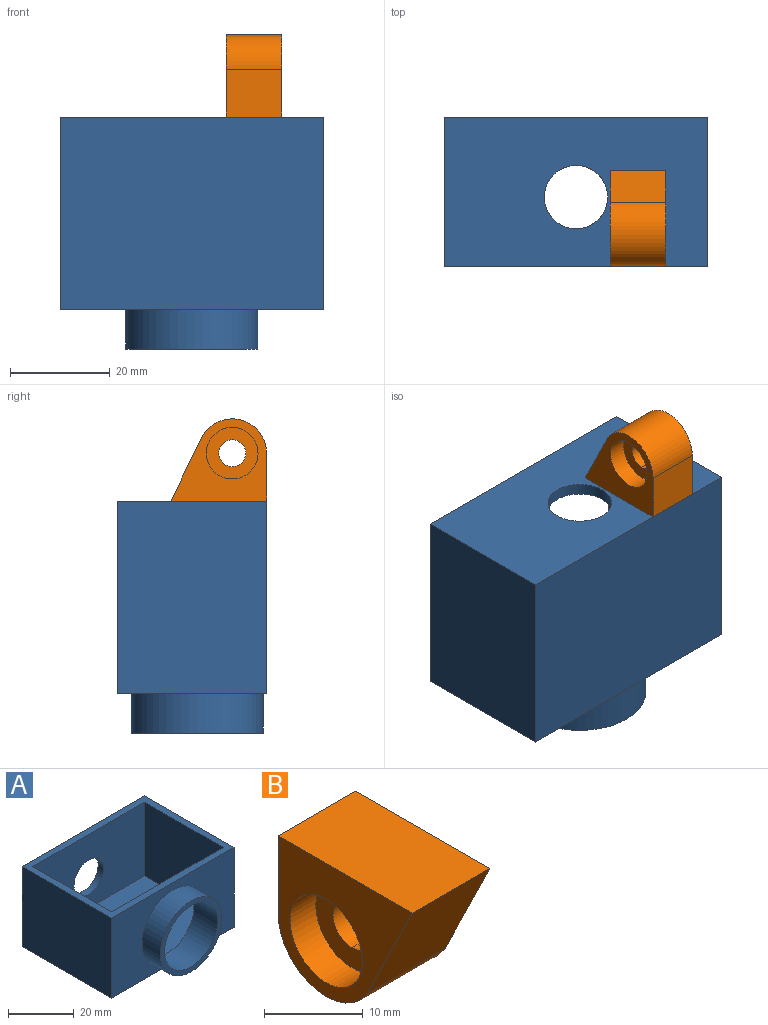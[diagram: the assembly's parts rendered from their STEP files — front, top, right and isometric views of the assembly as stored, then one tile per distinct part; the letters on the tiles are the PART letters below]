
ASSEMBLY  parts=2 mates=2
PART A: 15 faces, bbox 52.9x46.5x29.9 mm
  f0: plane 52.89x38.58mm, normal (0,0,-1), area 2040.9mm2, adj f4,f5,f6,f7
  f1: plane 33.92x27.56mm, normal (-1,0,0), area 934.8mm2, adj f2,f8,f9,f10
  f2: plane 48.23x27.56mm, normal (0,1,0), area 917.9mm2, adj f1,f3,f9,f10,f12
  f3: plane 33.92x27.56mm, normal (1,0,0), area 934.8mm2, adj f2,f8,f9,f10
  f4: plane 52.89x29.89mm, normal (0,-1,0), area 1029.6mm2, adj f0,f5,f7,f9,f13
  f5: plane 38.58x29.89mm, normal (1,0,0), area 1153.4mm2, adj f0,f4,f6,f9
  f6: plane 52.89x29.89mm, normal (0,1,0), area 1454mm2, adj f0,f5,f7,f9,f11
  f7: plane 38.58x29.89mm, normal (-1,0,0), area 1153.4mm2, adj f0,f4,f6,f9
  f8: plane 48.23x27.56mm, normal (0,-1,0), area 1202.1mm2, adj f1,f3,f9,f10,f11
  f9: plane 52.89x38.58mm, normal (0,0,1), area 404.9mm2, adj f1,f2,f3,f4,f5,f6,f7,f8
  f10: plane 48.23x33.92mm, normal (0,0,1), area 1636mm2, adj f1,f2,f3,f8
  f11: cylinder r=6.36mm len=12.72mm, axis (0,1,0), area 93.2mm2, adj f6,f8
  f12: cylinder r=11.44mm len=22.89mm, axis (0,1,0), area 739.2mm2, adj f2,f14
  f13: cylinder r=13.25mm len=26.5mm, axis (0,1,0), area 661.9mm2, adj f4,f14
  f14: plane 26.5x26.5mm, normal (0,-1,0), area 140.2mm2, adj f12,f13
PART B: 152 faces, bbox 11.1x19.2x16.5 mm
  f0: cylinder r=5.18mm len=10.37mm, axis (-1,0,0), area 120.8mm2, adj f148,f149
  f1: plane 12.72x12.72mm, normal (1,0,0), area 68.7mm2, adj f2,f3,f7,f8,f9,f10,f11,f13
  f2: cylinder r=2.7mm len=6.36mm, axis (1,0,0), area 54.2mm2, adj f1,f3,f149
  f3: cylinder r=2.7mm len=6.36mm, axis (1,0,0), area 54.2mm2, adj f1,f2,f149
  f4: plane 13.08x11.13mm, normal (0,-0.9,-0.44), area 162mm2, adj f5,f6,f148,f150
  f5: cylinder r=6.88mm len=12.82mm, axis (1,0,0), area 200mm2, adj f4,f6,f148,f151
  f6: plane 19.21x16.49mm, normal (1,0,0), area 110.1mm2, adj f4,f5,f7,f150,f151
  f7: cylinder r=6.36mm len=12.72mm, axis (1,0,0), area 42.4mm2, adj f1,f6
  f8: plane 1.06x0.85mm, normal (0,0,1), area 0.9mm2, adj f1,f9,f11,f12
  f9: plane 1.48x1.06mm, normal (0,1,0), area 1.6mm2, adj f1,f8,f10,f12
  f10: plane 1.06x0.85mm, normal (0,0,-1), area 0.9mm2, adj f1,f9,f11,f12
  f11: plane 1.48x1.06mm, normal (0,-1,0), area 1.6mm2, adj f1,f8,f10,f12
  f12: plane 1.48x0.85mm, normal (1,0,0), area 1.3mm2, adj f8,f9,f10,f11
  f13: plane 1.45x1.06mm, normal (0,-0.97,0.22), area 1.6mm2, adj f1,f14,f16,f17
  f14: plane 1.06x0.83mm, normal (0,0.22,0.97), area 0.9mm2, adj f1,f13,f15,f17
  f15: plane 1.45x1.06mm, normal (0,0.97,-0.22), area 1.6mm2, adj f1,f14,f16,f17
  f16: plane 1.06x0.83mm, normal (0,-0.22,-0.97), area 0.9mm2, adj f1,f13,f15,f17
  f17: plane 1.64x1.16mm, normal (1,0,0), area 1.3mm2, adj f13,f14,f15,f16
  f18: plane 1.34x1.06mm, normal (0,-0.9,0.43), area 1.6mm2, adj f1,f19,f21,f22
  f19: plane 1.06x0.76mm, normal (0,0.43,0.9), area 0.9mm2, adj f1,f18,f20,f22
  f20: plane 1.34x1.06mm, normal (0,0.9,-0.43), area 1.6mm2, adj f1,f19,f21,f22
  f21: plane 1.06x0.76mm, normal (0,-0.43,-0.9), area 0.9mm2, adj f1,f18,f20,f22
  f22: plane 1.71x1.41mm, normal (1,0,0), area 1.3mm2, adj f18,f19,f20,f21
  f23: plane 1.16x1.06mm, normal (0,-0.78,0.62), area 1.6mm2, adj f1,f24,f26,f27
  f24: plane 1.06x0.66mm, normal (0,0.62,0.78), area 0.9mm2, adj f1,f23,f25,f27
  f25: plane 1.16x1.06mm, normal (0,0.78,-0.62), area 1.6mm2, adj f1,f24,f26,f27
  f26: plane 1.06x0.66mm, normal (0,-0.62,-0.78), area 0.9mm2, adj f1,f23,f25,f27
  f27: plane 1.69x1.59mm, normal (1,0,0), area 1.3mm2, adj f23,f24,f25,f26
  f28: plane 1.16x1.06mm, normal (0,-0.62,0.78), area 1.6mm2, adj f1,f29,f31,f32
  f29: plane 1.06x0.66mm, normal (0,0.78,0.62), area 0.9mm2, adj f1,f28,f30,f32
  f30: plane 1.16x1.06mm, normal (0,0.62,-0.78), area 1.6mm2, adj f1,f29,f31,f32
  f31: plane 1.06x0.66mm, normal (0,-0.78,-0.62), area 0.9mm2, adj f1,f28,f30,f32
  f32: plane 1.69x1.59mm, normal (1,0,0), area 1.3mm2, adj f28,f29,f30,f31
  f33: plane 1.34x1.06mm, normal (0,-0.43,0.9), area 1.6mm2, adj f1,f34,f36,f37
  f34: plane 1.06x0.76mm, normal (0,0.9,0.43), area 0.9mm2, adj f1,f33,f35,f37
  f35: plane 1.34x1.06mm, normal (0,0.43,-0.9), area 1.6mm2, adj f1,f34,f36,f37
  f36: plane 1.06x0.76mm, normal (0,-0.9,-0.43), area 0.9mm2, adj f1,f33,f35,f37
  f37: plane 1.71x1.41mm, normal (1,0,0), area 1.3mm2, adj f33,f34,f35,f36
  f38: plane 1.45x1.06mm, normal (0,-0.22,0.97), area 1.6mm2, adj f1,f39,f41,f42
  f39: plane 1.06x0.83mm, normal (0,0.97,0.22), area 0.9mm2, adj f1,f38,f40,f42
  f40: plane 1.45x1.06mm, normal (0,0.22,-0.97), area 1.6mm2, adj f1,f39,f41,f42
  f41: plane 1.06x0.83mm, normal (0,-0.97,-0.22), area 0.9mm2, adj f1,f38,f40,f42
  f42: plane 1.64x1.16mm, normal (1,0,0), area 1.3mm2, adj f38,f39,f40,f41
  f43: plane 1.48x1.06mm, normal (0,0,1), area 1.6mm2, adj f1,f44,f46,f47
  f44: plane 1.06x0.85mm, normal (0,1,0), area 0.9mm2, adj f1,f43,f45,f47
  f45: plane 1.48x1.06mm, normal (0,0,-1), area 1.6mm2, adj f1,f44,f46,f47
  f46: plane 1.06x0.85mm, normal (0,-1,0), area 0.9mm2, adj f1,f43,f45,f47
  f47: plane 1.48x0.85mm, normal (1,0,0), area 1.3mm2, adj f43,f44,f45,f46
  f48: plane 1.45x1.06mm, normal (0,0.22,0.97), area 1.6mm2, adj f1,f49,f51,f52
  f49: plane 1.06x0.83mm, normal (0,0.97,-0.22), area 0.9mm2, adj f1,f48,f50,f52
  f50: plane 1.45x1.06mm, normal (0,-0.22,-0.97), area 1.6mm2, adj f1,f49,f51,f52
  f51: plane 1.06x0.83mm, normal (0,-0.97,0.22), area 0.9mm2, adj f1,f48,f50,f52
  f52: plane 1.64x1.16mm, normal (1,0,0), area 1.3mm2, adj f48,f49,f50,f51
  f53: plane 1.34x1.06mm, normal (0,0.43,0.9), area 1.6mm2, adj f1,f54,f56,f57
  f54: plane 1.06x0.76mm, normal (0,0.9,-0.43), area 0.9mm2, adj f1,f53,f55,f57
  f55: plane 1.34x1.06mm, normal (0,-0.43,-0.9), area 1.6mm2, adj f1,f54,f56,f57
  f56: plane 1.06x0.76mm, normal (0,-0.9,0.43), area 0.9mm2, adj f1,f53,f55,f57
  f57: plane 1.71x1.41mm, normal (1,0,0), area 1.3mm2, adj f53,f54,f55,f56
  f58: plane 1.16x1.06mm, normal (0,0.62,0.78), area 1.6mm2, adj f1,f59,f61,f62
  f59: plane 1.06x0.66mm, normal (0,0.78,-0.62), area 0.9mm2, adj f1,f58,f60,f62
  f60: plane 1.16x1.06mm, normal (0,-0.62,-0.78), area 1.6mm2, adj f1,f59,f61,f62
  f61: plane 1.06x0.66mm, normal (0,-0.78,0.62), area 0.9mm2, adj f1,f58,f60,f62
  f62: plane 1.69x1.59mm, normal (1,0,0), area 1.3mm2, adj f58,f59,f60,f61
  f63: plane 1.16x1.06mm, normal (0,0.78,0.62), area 1.6mm2, adj f1,f64,f66,f67
  f64: plane 1.06x0.66mm, normal (0,0.62,-0.78), area 0.9mm2, adj f1,f63,f65,f67
  f65: plane 1.16x1.06mm, normal (0,-0.78,-0.62), area 1.6mm2, adj f1,f64,f66,f67
  f66: plane 1.06x0.66mm, normal (0,-0.62,0.78), area 0.9mm2, adj f1,f63,f65,f67
  f67: plane 1.69x1.59mm, normal (1,0,0), area 1.3mm2, adj f63,f64,f65,f66
  f68: plane 1.34x1.06mm, normal (0,0.9,0.43), area 1.6mm2, adj f1,f69,f71,f72
  f69: plane 1.06x0.76mm, normal (0,0.43,-0.9), area 0.9mm2, adj f1,f68,f70,f72
  f70: plane 1.34x1.06mm, normal (0,-0.9,-0.43), area 1.6mm2, adj f1,f69,f71,f72
  f71: plane 1.06x0.76mm, normal (0,-0.43,0.9), area 0.9mm2, adj f1,f68,f70,f72
  f72: plane 1.71x1.41mm, normal (1,0,0), area 1.3mm2, adj f68,f69,f70,f71
  f73: plane 1.45x1.06mm, normal (0,0.97,0.22), area 1.6mm2, adj f1,f74,f76,f77
  f74: plane 1.06x0.83mm, normal (0,0.22,-0.97), area 0.9mm2, adj f1,f73,f75,f77
  f75: plane 1.45x1.06mm, normal (0,-0.97,-0.22), area 1.6mm2, adj f1,f74,f76,f77
  f76: plane 1.06x0.83mm, normal (0,-0.22,0.97), area 0.9mm2, adj f1,f73,f75,f77
  f77: plane 1.64x1.16mm, normal (1,0,0), area 1.3mm2, adj f73,f74,f75,f76
  f78: plane 1.48x1.06mm, normal (0,1,0), area 1.6mm2, adj f1,f79,f81,f82
  f79: plane 1.06x0.85mm, normal (0,0,-1), area 0.9mm2, adj f1,f78,f80,f82
  f80: plane 1.48x1.06mm, normal (0,-1,0), area 1.6mm2, adj f1,f79,f81,f82
  f81: plane 1.06x0.85mm, normal (0,0,1), area 0.9mm2, adj f1,f78,f80,f82
  f82: plane 1.48x0.85mm, normal (1,0,0), area 1.3mm2, adj f78,f79,f80,f81
  f83: plane 1.45x1.06mm, normal (0,0.97,-0.22), area 1.6mm2, adj f1,f84,f86,f87
  f84: plane 1.06x0.83mm, normal (0,-0.22,-0.97), area 0.9mm2, adj f1,f83,f85,f87
  f85: plane 1.45x1.06mm, normal (0,-0.97,0.22), area 1.6mm2, adj f1,f84,f86,f87
  f86: plane 1.06x0.83mm, normal (0,0.22,0.97), area 0.9mm2, adj f1,f83,f85,f87
  f87: plane 1.64x1.16mm, normal (1,0,0), area 1.3mm2, adj f83,f84,f85,f86
  f88: plane 1.34x1.06mm, normal (0,0.9,-0.43), area 1.6mm2, adj f1,f89,f91,f92
  f89: plane 1.06x0.76mm, normal (0,-0.43,-0.9), area 0.9mm2, adj f1,f88,f90,f92
  f90: plane 1.34x1.06mm, normal (0,-0.9,0.43), area 1.6mm2, adj f1,f89,f91,f92
  f91: plane 1.06x0.76mm, normal (0,0.43,0.9), area 0.9mm2, adj f1,f88,f90,f92
  f92: plane 1.71x1.41mm, normal (1,0,0), area 1.3mm2, adj f88,f89,f90,f91
  f93: plane 1.16x1.06mm, normal (0,0.78,-0.62), area 1.6mm2, adj f1,f94,f96,f97
  f94: plane 1.06x0.66mm, normal (0,-0.62,-0.78), area 0.9mm2, adj f1,f93,f95,f97
  f95: plane 1.16x1.06mm, normal (0,-0.78,0.62), area 1.6mm2, adj f1,f94,f96,f97
  f96: plane 1.06x0.66mm, normal (0,0.62,0.78), area 0.9mm2, adj f1,f93,f95,f97
  f97: plane 1.69x1.59mm, normal (1,0,0), area 1.3mm2, adj f93,f94,f95,f96
  f98: plane 1.16x1.06mm, normal (0,0.62,-0.78), area 1.6mm2, adj f1,f99,f101,f102
  f99: plane 1.06x0.66mm, normal (0,-0.78,-0.62), area 0.9mm2, adj f1,f98,f100,f102
  f100: plane 1.16x1.06mm, normal (0,-0.62,0.78), area 1.6mm2, adj f1,f99,f101,f102
  f101: plane 1.06x0.66mm, normal (0,0.78,0.62), area 0.9mm2, adj f1,f98,f100,f102
  f102: plane 1.69x1.59mm, normal (1,0,0), area 1.3mm2, adj f98,f99,f100,f101
  f103: plane 1.34x1.06mm, normal (0,0.43,-0.9), area 1.6mm2, adj f1,f104,f106,f107
  f104: plane 1.06x0.76mm, normal (0,-0.9,-0.43), area 0.9mm2, adj f1,f103,f105,f107
  f105: plane 1.34x1.06mm, normal (0,-0.43,0.9), area 1.6mm2, adj f1,f104,f106,f107
  f106: plane 1.06x0.76mm, normal (0,0.9,0.43), area 0.9mm2, adj f1,f103,f105,f107
  f107: plane 1.71x1.41mm, normal (1,0,0), area 1.3mm2, adj f103,f104,f105,f106
  f108: plane 1.45x1.06mm, normal (0,0.22,-0.97), area 1.6mm2, adj f1,f109,f111,f112
  f109: plane 1.06x0.83mm, normal (0,-0.97,-0.22), area 0.9mm2, adj f1,f108,f110,f112
  f110: plane 1.45x1.06mm, normal (0,-0.22,0.97), area 1.6mm2, adj f1,f109,f111,f112
  f111: plane 1.06x0.83mm, normal (0,0.97,0.22), area 0.9mm2, adj f1,f108,f110,f112
  f112: plane 1.64x1.16mm, normal (1,0,0), area 1.3mm2, adj f108,f109,f110,f111
  f113: plane 1.48x1.06mm, normal (0,0,-1), area 1.6mm2, adj f1,f114,f116,f117
  f114: plane 1.06x0.85mm, normal (0,-1,0), area 0.9mm2, adj f1,f113,f115,f117
  f115: plane 1.48x1.06mm, normal (0,0,1), area 1.6mm2, adj f1,f114,f116,f117
  f116: plane 1.06x0.85mm, normal (0,1,0), area 0.9mm2, adj f1,f113,f115,f117
  f117: plane 1.48x0.85mm, normal (1,0,0), area 1.3mm2, adj f113,f114,f115,f116
  f118: plane 1.45x1.06mm, normal (0,-0.22,-0.97), area 1.6mm2, adj f1,f119,f121,f122
  f119: plane 1.06x0.83mm, normal (0,-0.97,0.22), area 0.9mm2, adj f1,f118,f120,f122
  f120: plane 1.45x1.06mm, normal (0,0.22,0.97), area 1.6mm2, adj f1,f119,f121,f122
  f121: plane 1.06x0.83mm, normal (0,0.97,-0.22), area 0.9mm2, adj f1,f118,f120,f122
  f122: plane 1.64x1.16mm, normal (1,0,0), area 1.3mm2, adj f118,f119,f120,f121
  f123: plane 1.34x1.06mm, normal (0,-0.43,-0.9), area 1.6mm2, adj f1,f124,f126,f127
  f124: plane 1.06x0.76mm, normal (0,-0.9,0.43), area 0.9mm2, adj f1,f123,f125,f127
  f125: plane 1.34x1.06mm, normal (0,0.43,0.9), area 1.6mm2, adj f1,f124,f126,f127
  f126: plane 1.06x0.76mm, normal (0,0.9,-0.43), area 0.9mm2, adj f1,f123,f125,f127
  f127: plane 1.71x1.41mm, normal (1,0,0), area 1.3mm2, adj f123,f124,f125,f126
  f128: plane 1.16x1.06mm, normal (0,-0.62,-0.78), area 1.6mm2, adj f1,f129,f131,f132
  f129: plane 1.06x0.66mm, normal (0,-0.78,0.62), area 0.9mm2, adj f1,f128,f130,f132
  f130: plane 1.16x1.06mm, normal (0,0.62,0.78), area 1.6mm2, adj f1,f129,f131,f132
  f131: plane 1.06x0.66mm, normal (0,0.78,-0.62), area 0.9mm2, adj f1,f128,f130,f132
  f132: plane 1.69x1.59mm, normal (1,0,0), area 1.3mm2, adj f128,f129,f130,f131
  f133: plane 1.16x1.06mm, normal (0,-0.78,-0.62), area 1.6mm2, adj f1,f134,f136,f137
  f134: plane 1.06x0.66mm, normal (0,-0.62,0.78), area 0.9mm2, adj f1,f133,f135,f137
  f135: plane 1.16x1.06mm, normal (0,0.78,0.62), area 1.6mm2, adj f1,f134,f136,f137
  f136: plane 1.06x0.66mm, normal (0,0.62,-0.78), area 0.9mm2, adj f1,f133,f135,f137
  f137: plane 1.69x1.59mm, normal (1,0,0), area 1.3mm2, adj f133,f134,f135,f136
  f138: plane 1.34x1.06mm, normal (0,-0.9,-0.43), area 1.6mm2, adj f1,f139,f141,f142
  f139: plane 1.06x0.76mm, normal (0,-0.43,0.9), area 0.9mm2, adj f1,f138,f140,f142
  f140: plane 1.34x1.06mm, normal (0,0.9,0.43), area 1.6mm2, adj f1,f139,f141,f142
  f141: plane 1.06x0.76mm, normal (0,0.43,-0.9), area 0.9mm2, adj f1,f138,f140,f142
  f142: plane 1.71x1.41mm, normal (1,0,0), area 1.3mm2, adj f138,f139,f140,f141
  f143: plane 1.45x1.06mm, normal (0,-0.97,-0.22), area 1.6mm2, adj f1,f144,f146,f147
  f144: plane 1.06x0.83mm, normal (0,-0.22,0.97), area 0.9mm2, adj f1,f143,f145,f147
  f145: plane 1.45x1.06mm, normal (0,0.97,0.22), area 1.6mm2, adj f1,f144,f146,f147
  f146: plane 1.06x0.83mm, normal (0,0.22,-0.97), area 0.9mm2, adj f1,f143,f145,f147
  f147: plane 1.64x1.16mm, normal (1,0,0), area 1.3mm2, adj f143,f144,f145,f146
  f148: plane 19.21x16.49mm, normal (-1,0,0), area 152.8mm2, adj f0,f4,f5,f150,f151
  f149: plane 10.37x10.37mm, normal (-1,0,0), area 61.3mm2, adj f0,f2,f3
  f150: plane 19.21x11.13mm, normal (0,0,1), area 213.8mm2, adj f4,f6,f148,f151
  f151: plane 11.13x9.6mm, normal (0,1,0), area 106.9mm2, adj f5,f6,f148,f150
PLACE A rot(axis=(0,-0.71,-0.71),180deg) t=(24.5,51.17,35.15)mm
PLACE B rot(axis=(1,0,0),180deg) t=(93.33,53.86,52.11)mm
MATE planar A.f6 <-> B.f150  axis (0,0,1) through (-1.95,63.78,54.44)mm
MATE planar B.f151 <-> A.f0  axis (0,-1,0) through (36.97,48.84,59.24)mm
